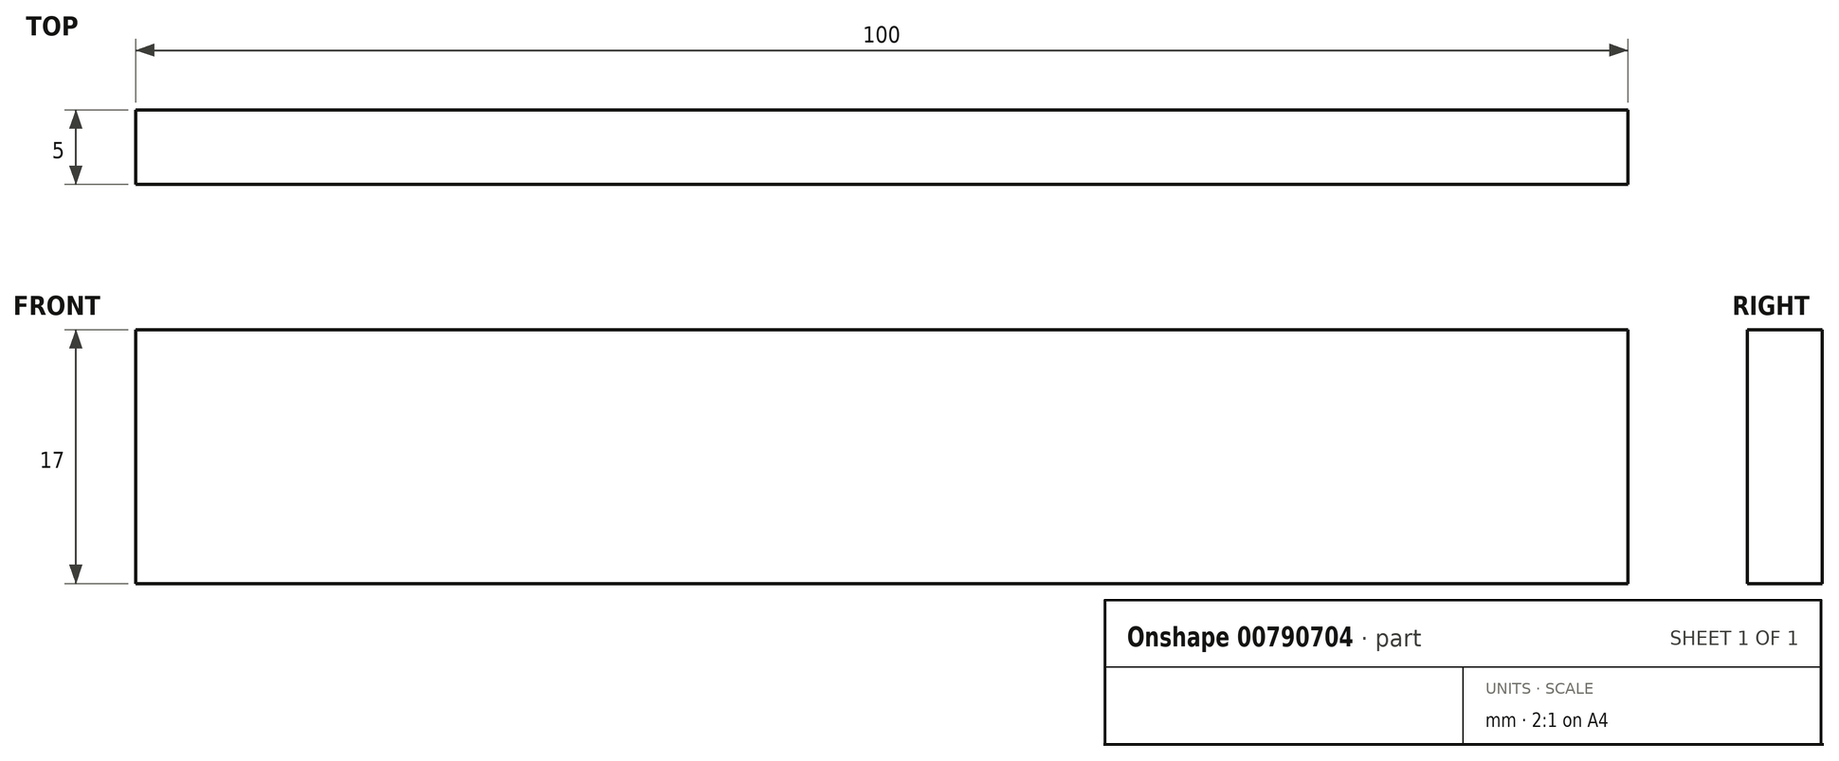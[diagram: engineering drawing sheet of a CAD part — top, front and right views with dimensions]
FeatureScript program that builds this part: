
annotation { "Feature Type Name" : "Feature", "Feature Type Description" : "" }
export const myFeature = defineFeature(function(context is Context, id is Id, definition is map)
    precondition{}
    {
        {
            var Q0;
            Q0=qCreatedBy(makeId("Top.planeOp"),FACE);
            var sketch = newSketch(context, id + "F0", { "sketchPlane" : qUnion([Q0])});
            skLineSegment(sketch, "E0.bottom", {"start": v(50, 2.5) * mm, "end": v(-50, 2.5) * mm});
            skLineSegment(sketch, "E0.top", {"start": v(50, -2.5) * mm, "end": v(-50, -2.5) * mm});
            skLineSegment(sketch, "E0.left", {"start": v(50, 2.5) * mm, "end": v(50, -2.5) * mm});
            skLineSegment(sketch, "E0.right", {"start": v(-50, 2.5) * mm, "end": v(-50, -2.5) * mm});
            skPoint(sketch, "E0.middle", {"position": v(0, 0) * mm});
            skSolve(sketch);
        }
        {
            var Q0;
            Q0=makeQuery(id+"F0.imprint","IMPRINT",FACE,{"disambiguationData":[TD([[makeQuery(id+"F0.imprint","IMPRINT",EDGE,{"derivedFrom":sQuery(id+"F0.wireOp",EDGE,"E0.bottom")}),1.0]])]});
            extrude(context, id + "F1", {"entities" : qUnion([Q0]), "depth" : 17 * mm, "offsetDistance" : 25 * mm});
        }
    });
